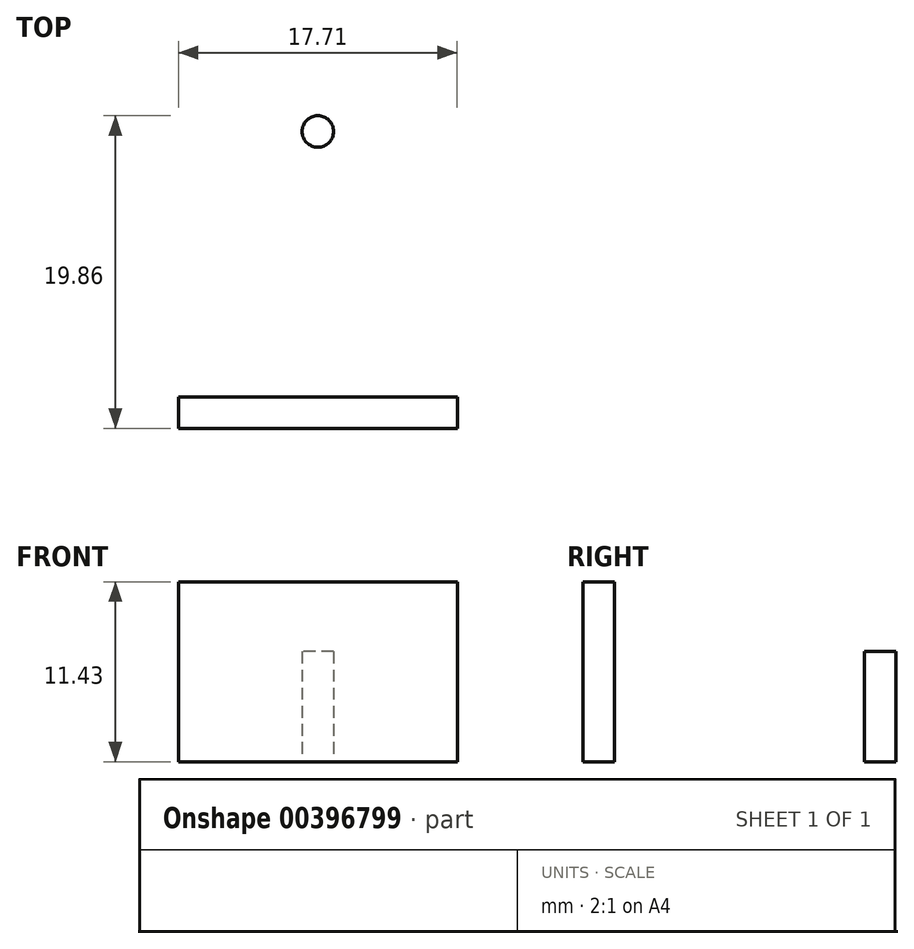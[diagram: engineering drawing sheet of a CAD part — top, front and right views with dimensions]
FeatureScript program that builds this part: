
annotation { "Feature Type Name" : "Feature", "Feature Type Description" : "" }
export const myFeature = defineFeature(function(context is Context, id is Id, definition is map)
    precondition{}
    {
        {
            assignVariable(context, id + "F0", {"name" : "Size", "anyValue" : 17.5});
        }
        {
            var Q0;
            Q0=qCreatedBy(makeId("Top.planeOp"),FACE);
            var sketch = newSketch(context, id + "F1", { "sketchPlane" : qUnion([Q0])});
            skLineSegment(sketch, "E0.bottom", {"start": v(0, 0) * mm, "end": v(17.71, 0) * mm});
            skLineSegment(sketch, "E0.top", {"start": v(0, 2) * mm, "end": v(17.71, 2) * mm});
            skLineSegment(sketch, "E0.left", {"start": v(0, 0) * mm, "end": v(0, 2) * mm});
            skLineSegment(sketch, "E0.right", {"start": v(17.71, 0) * mm, "end": v(17.71, 2) * mm});
            skLineSegment(sketch, "E1.bottom", {"start": v(7.36, 2) * mm, "end": v(10.36, 2) * mm});
            skLineSegment(sketch, "E1.top", {"start": v(7.36, 20.86) * mm, "end": v(10.36, 20.86) * mm});
            skLineSegment(sketch, "E1.left", {"start": v(7.36, 2) * mm, "end": v(7.36, 20.86) * mm});
            skLineSegment(sketch, "E1.right", {"start": v(10.36, 2) * mm, "end": v(10.36, 20.86) * mm});
            skLineSegment(sketch, "E2", {"start": v(8.86, 0) * mm, "end": v(8.86, 20.86) * mm, "construction": true});
            skCircle(sketch, "E3", {"center": v(8.86, 18.86) * mm, "radius": 1 * mm});
            skSolve(sketch);
        }
        {
            var Q0;
            Q0=makeQuery(id+"F1.imprint","IMPRINT",FACE,{"disambiguationData":[TD([[makeQuery(id+"F1.imprint","IMPRINT",EDGE,{"derivedFrom":sQuery(id+"F1.wireOp",EDGE,"E3")}),1.0]])]});
            var Q1;
            Q1=makeQuery(id+"F1.imprint","IMPRINT",FACE,{"disambiguationData":[TD([[makeQuery(id+"F1.imprint","IMPRINT",EDGE,{"derivedFrom":sQuery(id+"F1.wireOp",EDGE,"E1.bottom")}),1.0]])]});
            var Q2;
            Q2=makeQuery(id+"F1.imprint","IMPRINT",FACE,{"disambiguationData":[TD([[makeQuery(id+"F1.imprint","IMPRINT",EDGE,{"derivedFrom":sQuery(id+"F1.wireOp",EDGE,"E0.bottom")}),1.0]])]});
            extrude(context, id + "F2", {"entities" : qUnion([Q0, Q1, Q2]), "depth" : 3 * mm});
        }
        {
            var Q0;
            Q0=makeQuery(id+"F1.imprint","IMPRINT",FACE,{"disambiguationData":[TD([[makeQuery(id+"F1.imprint","IMPRINT",EDGE,{"derivedFrom":sQuery(id+"F1.wireOp",EDGE,"E0.bottom")}),1.0]])]});
            extrude(context, id + "F3", {"entities" : qUnion([Q0]), "operationType" : NewBodyOperationType.ADD, "depth" : (200 / getVariable(context, 'Size')) * mm});
        }
        {
            var Q0;
            Q0=makeQuery(id+"F1.imprint","IMPRINT",FACE,{"disambiguationData":[TD([[makeQuery(id+"F1.imprint","IMPRINT",EDGE,{"derivedFrom":sQuery(id+"F1.wireOp",EDGE,"E3")}),1.0]])]});
            extrude(context, id + "F4", {"entities" : qUnion([Q0]), "operationType" : NewBodyOperationType.ADD, "depth" : 7 * mm});
        }
    });
